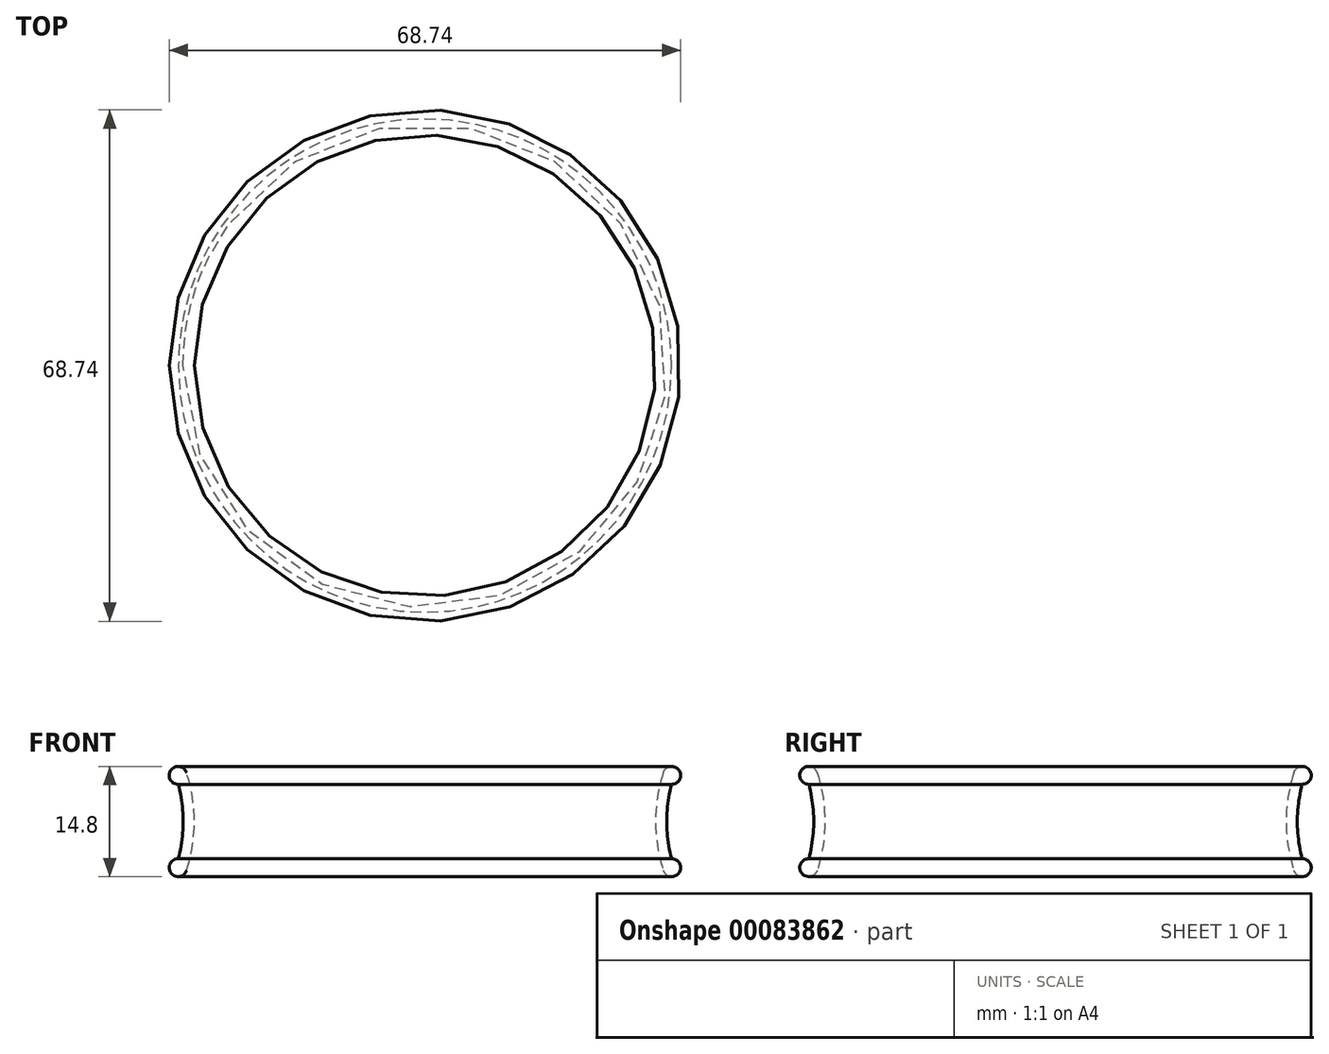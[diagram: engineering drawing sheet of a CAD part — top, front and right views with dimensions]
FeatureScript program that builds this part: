
annotation { "Feature Type Name" : "Feature", "Feature Type Description" : "" }
export const myFeature = defineFeature(function(context is Context, id is Id, definition is map)
    precondition{}
    {
        {
            var Q0;
            Q0=qCreatedBy(makeId("Front.planeOp"),FACE);
            var sketch = newSketch(context, id + "F0", { "sketchPlane" : qUnion([Q0])});
            skLineSegment(sketch, "E0", {"start": v(0, 0) * mm, "end": v(0, 34) * mm, "construction": true});
            skArc(sketch, "E1", {"start": v(-32.5, 0) * mm, "mid": v(-32.66, 2.52) * mm, "end": v(-33.14, 5) * mm});
            skLineSegment(sketch, "E2", {"start": v(0, 0) * mm, "end": v(-68.18, 0) * mm, "construction": true});
            skArc(sketch, "E3", {"start": v(-33.14, 5) * mm, "mid": v(-34.15, 6.9) * mm, "end": v(-32.03, 6.57) * mm});
            skArc(sketch, "E4", {"start": v(-31, 0) * mm, "mid": v(-31.26, 3.32) * mm, "end": v(-32.03, 6.57) * mm});
            skArc(sketch, "E5.MirrorCS", {"start": v(-33.14, -5) * mm, "mid": v(-34.15, -6.9) * mm, "end": v(-32.03, -6.57) * mm});
            skArc(sketch, "E6.MirrorCS", {"start": v(-31, 0) * mm, "mid": v(-31.26, -3.32) * mm, "end": v(-32.03, -6.57) * mm});
            skArc(sketch, "E7.MirrorCS", {"start": v(-32.5, 0) * mm, "mid": v(-32.66, -2.52) * mm, "end": v(-33.14, -5) * mm});
            skSolve(sketch);
        }
        {
            var Q0;
            Q0 = qSketchRegion(id + "F0", true);
            var Q1;
            Q1=sQuery(id+"F0.wireOp",EDGE,"E0");
            revolve(context, id + "F1", {"entities" : qUnion([Q0]), "axis" : qUnion([Q1]), "revolveType" : RevolveType.FULL});
        }
    });
